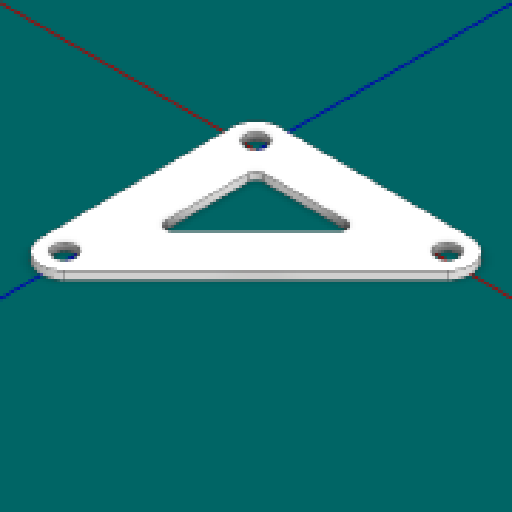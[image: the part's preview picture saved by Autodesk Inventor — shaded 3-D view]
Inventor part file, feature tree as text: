
AUTODESK INVENTOR PART (.ipt)
format: ipt  version: 2025 (Build 290162000, 162)  size: 123,904 bytes
history: native  units: in
note: dims shown in document units (in); Inventor stores cm internally (conversion verified against a paired STEP export)
features: other x3, extrude x1, sketch x1
ambient origin geometry x8: Origin, YZ Plane, XZ Plane, XY Plane, X Axis, Y Axis, Z Axis, Center Point
bodies: Solid1 (feature_tree)
feature tree (5):
  other  "Blocks"
  extrude  "Extrusion1"  Depth=0.375in
  sketch  "Sketch1"  dims[d0=0.375in d1=0.375in d2=0.375in d3=0.0625in d4=0.0in d5=0.375in d6=0.0625in d7=0.0625in]
  other  "main"
  other  "main:1"
